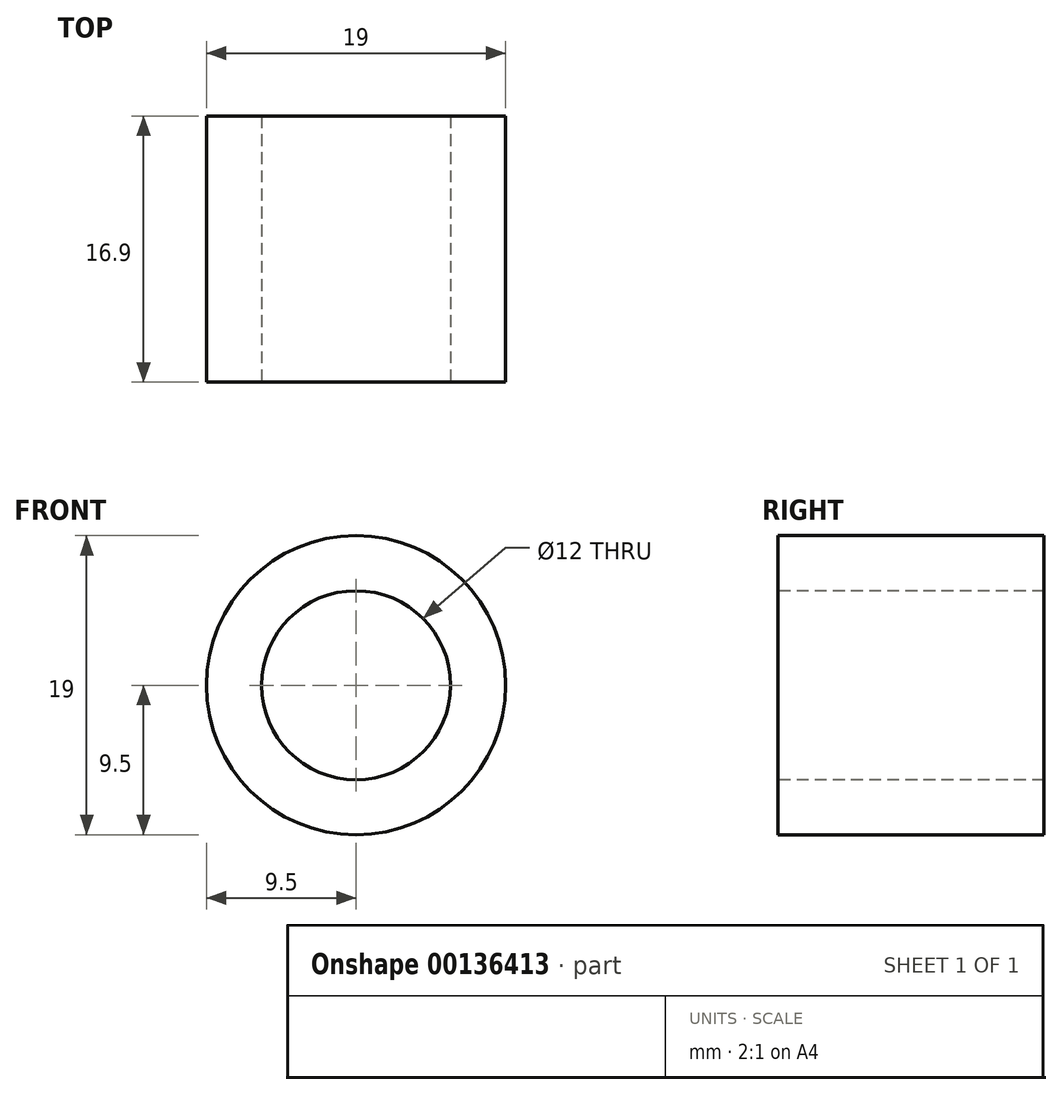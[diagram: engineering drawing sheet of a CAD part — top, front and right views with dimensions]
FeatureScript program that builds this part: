
annotation { "Feature Type Name" : "Feature", "Feature Type Description" : "" }
export const myFeature = defineFeature(function(context is Context, id is Id, definition is map)
    precondition{}
    {
        {
            var Q0;
            Q0=qCreatedBy(makeId("Front.planeOp"),FACE);
            var sketch = newSketch(context, id + "F0", { "sketchPlane" : qUnion([Q0])});
            skCircle(sketch, "E0", {"center": v(0, 0) * mm, "radius": 6 * mm});
            skCircle(sketch, "E1", {"center": v(0, 0) * mm, "radius": 9.5 * mm});
            skSolve(sketch);
        }
        {
            var Q0;
            Q0=makeQuery(id+"F0.imprint","IMPRINT",FACE,{"disambiguationData":[TD([[makeQuery(id+"F0.imprint","IMPRINT",EDGE,{"derivedFrom":sQuery(id+"F0.wireOp",EDGE,"E0")}),-1.0]])]});
            extrude(context, id + "F1", {"entities" : qUnion([Q0]), "oppositeDirection" : true, "depth" : 16.9 * mm});
        }
    });
